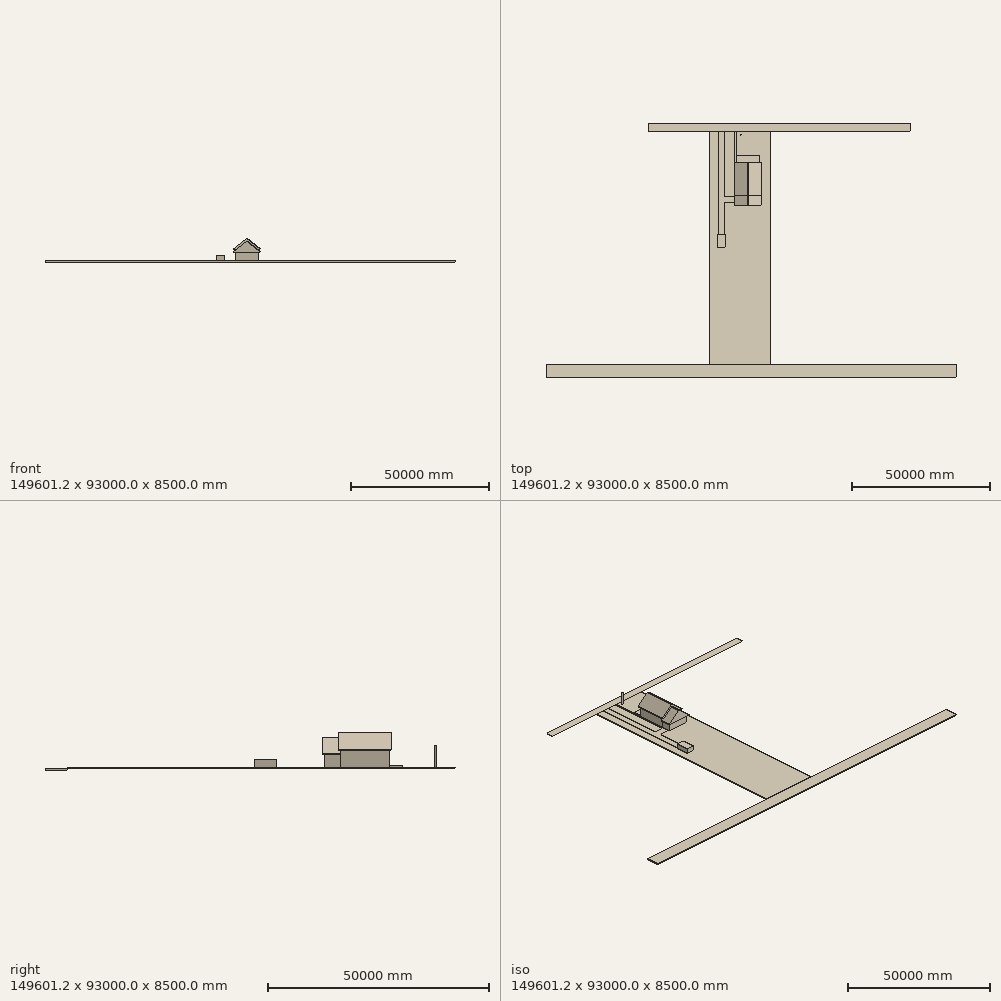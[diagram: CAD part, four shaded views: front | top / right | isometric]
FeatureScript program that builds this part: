
annotation { "Feature Type Name" : "Feature", "Feature Type Description" : "" }
export const myFeature = defineFeature(function(context is Context, id is Id, definition is map)
    precondition{}
    {
        {
            var Q0;
            Q0=qCreatedBy(makeId("Top.planeOp"),FACE);
            var sketch = newSketch(context, id + "F0", { "sketchPlane" : qUnion([Q0])});
            skLineSegment(sketch, "E0.bottom", {"start": v(-22500, 0) * mm, "end": v(0, 0) * mm});
            skLineSegment(sketch, "E0.top", {"start": v(-22500, -85000) * mm, "end": v(0, -85000) * mm});
            skLineSegment(sketch, "E0.left", {"start": v(-22500, 0) * mm, "end": v(-22500, -85000) * mm});
            skLineSegment(sketch, "E0.right", {"start": v(0, 0) * mm, "end": v(0, -85000) * mm});
            skLineSegment(sketch, "E1.bottom", {"start": v(-12540, -12000) * mm, "end": v(-4000, -12000) * mm});
            skLineSegment(sketch, "E1.top", {"start": v(-12540, -26660) * mm, "end": v(-4000, -26660) * mm});
            skLineSegment(sketch, "E1.left", {"start": v(-12540, -12000) * mm, "end": v(-12540, -26660) * mm});
            skLineSegment(sketch, "E1.right", {"start": v(-4000, -12000) * mm, "end": v(-4000, -26660) * mm});
            skLineSegment(sketch, "E2.bottom", {"start": v(-44660.48, 3000) * mm, "end": v(50787.96, 3000) * mm});
            skLineSegment(sketch, "E2.top", {"start": v(-44660.48, 0) * mm, "end": v(50787.96, 0) * mm});
            skLineSegment(sketch, "E2.left", {"start": v(-44660.48, 3000) * mm, "end": v(-44660.48, 0) * mm});
            skLineSegment(sketch, "E2.right", {"start": v(50787.96, 3000) * mm, "end": v(50787.96, 0) * mm});
            skLineSegment(sketch, "E3.bottom", {"start": v(-81843.28, -90000) * mm, "end": v(67757.95, -90000) * mm});
            skLineSegment(sketch, "E3.top", {"start": v(-81843.28, -85000) * mm, "end": v(67757.95, -85000) * mm});
            skLineSegment(sketch, "E3.left", {"start": v(-81843.28, -90000) * mm, "end": v(-81843.28, -85000) * mm});
            skLineSegment(sketch, "E3.right", {"start": v(67757.95, -90000) * mm, "end": v(67757.95, -85000) * mm});
            skCircle(sketch, "E4", {"center": v(-11000, -1500) * mm, "radius": 250 * mm});
            skLineSegment(sketch, "E5", {"start": v(0, -42500) * mm, "end": v(-22500, -42500) * mm});
            skLineSegment(sketch, "E6.bottom", {"start": v(-19500, -42500) * mm, "end": v(-16500, -42500) * mm});
            skLineSegment(sketch, "E6.top", {"start": v(-19500, -37500) * mm, "end": v(-16500, -37500) * mm});
            skLineSegment(sketch, "E6.left", {"start": v(-19500, -42500) * mm, "end": v(-19500, -37500) * mm});
            skLineSegment(sketch, "E6.right", {"start": v(-16500, -42500) * mm, "end": v(-16500, -37500) * mm});
            skLineSegment(sketch, "E7.bottom", {"start": v(-19250, 0) * mm, "end": v(-16750, 0) * mm});
            skLineSegment(sketch, "E7.top", {"start": v(-19250, -37500) * mm, "end": v(-16750, -37500) * mm});
            skLineSegment(sketch, "E7.left", {"start": v(-19250, 0) * mm, "end": v(-19250, -37500) * mm});
            skLineSegment(sketch, "E7.right", {"start": v(-16750, 0) * mm, "end": v(-16750, -37500) * mm});
            skLineSegment(sketch, "E8.bottom", {"start": v(-12540, -23620) * mm, "end": v(-16750, -23620) * mm});
            skLineSegment(sketch, "E8.top", {"start": v(-12540, -26120) * mm, "end": v(-16750, -26120) * mm});
            skLineSegment(sketch, "E8.left", {"start": v(-12540, -23620) * mm, "end": v(-12540, -26120) * mm});
            skLineSegment(sketch, "E8.right", {"start": v(-16750, -23620) * mm, "end": v(-16750, -26120) * mm});
            skLineSegment(sketch, "E9.top", {"start": v(-12540, -9000) * mm, "end": v(-4000, -9000) * mm});
            skLineSegment(sketch, "E9.left", {"start": v(-12540, -12000) * mm, "end": v(-12540, -9000) * mm});
            skLineSegment(sketch, "E9.right", {"start": v(-4000, -12000) * mm, "end": v(-4000, -9000) * mm});
            skLineSegment(sketch, "E10.bottom", {"start": v(-12540, -23620) * mm, "end": v(-13240, -23620) * mm});
            skLineSegment(sketch, "E10.top", {"start": v(-12540, 0) * mm, "end": v(-13240, 0) * mm});
            skLineSegment(sketch, "E10.left", {"start": v(-12540, -23620) * mm, "end": v(-12540, 0) * mm});
            skLineSegment(sketch, "E10.right", {"start": v(-13240, -23620) * mm, "end": v(-13240, 0) * mm});
            skLineSegment(sketch, "E11", {"start": v(-12540, -23080) * mm, "end": v(-4000, -23080) * mm});
            skSolve(sketch);
        }
        {
            var Q0;
            {var subQ2=sQuery(id+"F0.wireOp",EDGE,"E6.left");Q0=makeQuery(id+"F0.imprint","IMPRINT",FACE,{"disambiguationData":[TD([[makeQuery(id+"F0.imprint","IMPRINT",EDGE,{"derivedFrom":subQ2}),1.0]])]});}
            var Q1;
            {var subQ3=sQuery(id+"F0.wireOp",EDGE,"E10.right");Q1=makeQuery(id+"F0.imprint","IMPRINT",FACE,{"disambiguationData":[TD([[makeQuery(id+"F0.imprint","IMPRINT",EDGE,{"derivedFrom":subQ3}),1.0]])]});}
            var Q2;
            {var subQ5=sQuery(id+"F0.wireOp",EDGE,"E1.top");Q2=makeQuery(id+"F0.imprint","IMPRINT",FACE,{"disambiguationData":[TD([[makeQuery(id+"F0.imprint","IMPRINT",EDGE,{"derivedFrom":subQ5}),-1.0]])]});}
            var Q3;
            {var subQ5=sQuery(id+"F0.wireOp",EDGE,"E0.top");Q3=makeQuery(id+"F0.imprint","IMPRINT",FACE,{"disambiguationData":[TD([[makeQuery(id+"F0.imprint","IMPRINT",EDGE,{"derivedFrom":subQ5}),1.0]])]});}
            extrude(context, id + "F1", {"entities" : qUnion([Q0, Q1, Q2, Q3]), "depth" : 100 * mm, "offsetDistance" : 25 * mm});
        }
        {
            var Q0;
            {var subQ0=sQuery(id+"F0.wireOp",EDGE,"E7.left");Q0=makeQuery(id+"F0.imprint","IMPRINT",FACE,{"disambiguationData":[TD([[makeQuery(id+"F0.imprint","IMPRINT",EDGE,{"derivedFrom":subQ0}),1.0]])]});}
            var Q1;
            {var subQ4=sQuery(id+"F0.wireOp",EDGE,"E9.left");Q1=makeQuery(id+"F0.imprint","IMPRINT",FACE,{"disambiguationData":[TD([[makeQuery(id+"F0.imprint","IMPRINT",EDGE,{"derivedFrom":subQ4}),1.0]])]});}
            var Q2;
            {var subQ6=sQuery(id+"F0.wireOp",EDGE,"E8.top");Q2=makeQuery(id+"F0.imprint","IMPRINT",FACE,{"disambiguationData":[TD([[makeQuery(id+"F0.imprint","IMPRINT",EDGE,{"derivedFrom":subQ6}),-1.0]])]});}
            extrude(context, id + "F2", {"entities" : qUnion([Q0, Q1, Q2]), "depth" : 100 * mm, "offsetDistance" : 25 * mm});
        }
        {
            var Q0;
            {var subQ2=sQuery(id+"F0.wireOp",EDGE,"E6.left");Q0=makeQuery(id+"F0.imprint","IMPRINT",FACE,{"disambiguationData":[TD([[makeQuery(id+"F0.imprint","IMPRINT",EDGE,{"derivedFrom":subQ2}),-1.0]])]});}
            extrude(context, id + "F3", {"entities" : qUnion([Q0]), "depth" : 2000 * mm, "offsetDistance" : 25 * mm});
        }
        {
            var Q0;
            Q0=makeQuery(id+"F0.imprint","IMPRINT",FACE,{"disambiguationData":[TD([[makeQuery(id+"F0.imprint","IMPRINT",EDGE,{"derivedFrom":sQuery(id+"F0.wireOp",EDGE,"E4")}),1.0]])]});
            extrude(context, id + "F4", {"entities" : qUnion([Q0]), "depth" : 5000 * mm, "offsetDistance" : 25 * mm});
        }
        {
            var Q0;
            {var subQ1=sQuery(id+"F0.wireOp",EDGE,"E1.top");Q0=makeQuery(id+"F0.imprint","IMPRINT",FACE,{"disambiguationData":[TD([[makeQuery(id+"F0.imprint","IMPRINT",EDGE,{"derivedFrom":subQ1}),1.0]])]});}
            extrude(context, id + "F5", {"entities" : qUnion([Q0]), "depth" : 3000 * mm, "offsetDistance" : 25 * mm});
        }
        {
            var Q0;
            Q0=makeQuery(id+"F0.imprint","IMPRINT",FACE,{"disambiguationData":[TD([[makeQuery(id+"F0.imprint","IMPRINT",EDGE,{"derivedFrom":sQuery(id+"F0.wireOp",EDGE,"E1.bottom")}),1.0]])]});
            extrude(context, id + "F6", {"entities" : qUnion([Q0]), "depth" : 500 * mm, "offsetDistance" : 25 * mm});
        }
        {
            var Q0;
            {var subQ0=sQuery(id+"F0.wireOp",EDGE,"E1.bottom");Q0=makeQuery(id+"F0.imprint","IMPRINT",FACE,{"disambiguationData":[TD([[makeQuery(id+"F0.imprint","IMPRINT",EDGE,{"derivedFrom":subQ0}),-1.0]])]});}
            extrude(context, id + "F7", {"entities" : qUnion([Q0]), "depth" : 4000 * mm, "offsetDistance" : 25 * mm});
        }
        {
            var Q0;
            {var subQ1=sQuery(id+"F0.wireOp",EDGE,"E0.top");Q0=makeQuery(id+"F0.imprint","IMPRINT",FACE,{"disambiguationData":[TD([[makeQuery(id+"F0.imprint","IMPRINT",EDGE,{"derivedFrom":subQ1}),-1.0]])]});}
            extrude(context, id + "F8", {"entities" : qUnion([Q0]), "oppositeDirection" : true, "depth" : 500 * mm, "offsetDistance" : 25 * mm});
        }
        {
            var Q0;
            Q0=makeQuery(id+"F0.imprint","IMPRINT",FACE,{"disambiguationData":[TD([[makeQuery(id+"F0.imprint","IMPRINT",EDGE,{"derivedFrom":sQuery(id+"F0.wireOp",EDGE,"E2.bottom")}),-1.0]])]});
            extrude(context, id + "F9", {"entities" : qUnion([Q0]), "depth" : 100 * mm, "offsetDistance" : 25 * mm});
        }
        {
            var Q0;
            Q0=makeQuery(id+"F7.opExtrude","CAP_FACE",FACE,{"disambiguationData":[OSD([sQuery(id+"F0.wireOp",EDGE,"E1.bottom"),sQuery(id+"F0.wireOp",EDGE,"E1.left"),sQuery(id+"F0.wireOp",EDGE,"E1.right"),sQuery(id+"F0.wireOp",EDGE,"E11")])],"isStart":false});
            var sketch = newSketch(context, id + "F10", { "sketchPlane" : qUnion([Q0])});
            skLineSegment(sketch, "E12.bottom", {"start": v(-13240, -11500) * mm, "end": v(-3300, -11500) * mm});
            skLineSegment(sketch, "E12.top", {"start": v(-13240, -23580) * mm, "end": v(-3300, -23580) * mm});
            skLineSegment(sketch, "E12.left", {"start": v(-13240, -11500) * mm, "end": v(-13240, -23580) * mm});
            skLineSegment(sketch, "E12.right", {"start": v(-3300, -11500) * mm, "end": v(-3300, -23580) * mm});
            skSolve(sketch);
        }
        {
            var Q0;
            Q0=makeQuery(id+"F10.imprint","IMPRINT",FACE,{"disambiguationData":[TD([[makeQuery(id+"F10.imprint","IMPRINT",EDGE,{"derivedFrom":sQuery(id+"F10.wireOp",EDGE,"E12.bottom")}),-1.0]])]});
            var Q1;
            Q1=makeQuery(id+"F10.imprint","IMPRINT",FACE,{"disambiguationData":[TD([[makeQuery(id+"F10.imprint","IMPRINT",EDGE,{"derivedFrom":makeQuery(id+"F7.opExtrude","CAP_EDGE",EDGE,{"disambiguationData":[OSD([sQuery(id+"F0.wireOp",EDGE,"E1.bottom")])],"isStart":false})}),-1.0]])]});
            extrude(context, id + "F11", {"entities" : qUnion([Q0, Q1]), "depth" : 4000 * mm, "offsetDistance" : 25 * mm});
        }
        {
            var Q0;
            Q0=makeQuery(id+"F11.opExtrude","CAP_EDGE",EDGE,{"disambiguationData":[OSD([sQuery(id+"F10.wireOp",EDGE,"E12.left")])],"isStart":false});
            var Q1;
            Q1=makeQuery(id+"F11.opExtrude","CAP_EDGE",EDGE,{"disambiguationData":[OSD([sQuery(id+"F10.wireOp",EDGE,"E12.right")])],"isStart":false});
            chamfer(context, id + "F12", {"entities" : qUnion([Q0, Q1]), "chamferType" : ChamferType.TWO_OFFSETS, "width1" : 4800 * mm, "oppositeDirection" : false, "width2" : 3800 * mm, "tangentPropagation" : true});
        }
        {
            var Q0;
            Q0=makeQuery(id+"F5.opExtrude","CAP_FACE",FACE,{"disambiguationData":[OSD([sQuery(id+"F0.wireOp",EDGE,"E1.top"),sQuery(id+"F0.wireOp",EDGE,"E1.left"),sQuery(id+"F0.wireOp",EDGE,"E1.right"),sQuery(id+"F0.wireOp",EDGE,"E11")])],"isStart":false});
            var sketch = newSketch(context, id + "F13", { "sketchPlane" : qUnion([Q0])});
            skLineSegment(sketch, "E13.bottom", {"start": v(-13240, -23080) * mm, "end": v(-3300, -23080) * mm});
            skLineSegment(sketch, "E13.top", {"start": v(-13240, -27160) * mm, "end": v(-3300, -27160) * mm});
            skLineSegment(sketch, "E13.left", {"start": v(-13240, -23080) * mm, "end": v(-13240, -27160) * mm});
            skLineSegment(sketch, "E13.right", {"start": v(-3300, -23080) * mm, "end": v(-3300, -27160) * mm});
            skSolve(sketch);
        }
        {
            var Q0;
            Q0=makeQuery(id+"F13.imprint","IMPRINT",FACE,{"disambiguationData":[TD([[makeQuery(id+"F13.imprint","IMPRINT",EDGE,{"derivedFrom":makeQuery(id+"F5.opExtrude","CAP_EDGE",EDGE,{"disambiguationData":[OSD([sQuery(id+"F0.wireOp",EDGE,"E1.top")])],"isStart":false})}),1.0]])]});
            var Q1;
            Q1=makeQuery(id+"F13.imprint","IMPRINT",FACE,{"disambiguationData":[TD([[makeQuery(id+"F13.imprint","IMPRINT",EDGE,{"derivedFrom":sQuery(id+"F13.wireOp",EDGE,"E13.top")}),1.0]])]});
            extrude(context, id + "F14", {"entities" : qUnion([Q0, Q1]), "depth" : 4000 * mm, "offsetDistance" : 25 * mm});
        }
        {
            var Q0;
            Q0=makeQuery(id+"F14.opExtrude","CAP_EDGE",EDGE,{"disambiguationData":[OSD([sQuery(id+"F13.wireOp",EDGE,"E13.left")])],"isStart":false});
            var Q1;
            Q1=makeQuery(id+"F14.opExtrude","CAP_EDGE",EDGE,{"disambiguationData":[OSD([sQuery(id+"F13.wireOp",EDGE,"E13.right")])],"isStart":false});
            chamfer(context, id + "F15", {"entities" : qUnion([Q0, Q1]), "chamferType" : ChamferType.TWO_OFFSETS, "width1" : 4800 * mm, "oppositeDirection" : false, "width2" : 3800 * mm, "tangentPropagation" : true});
        }
    });
